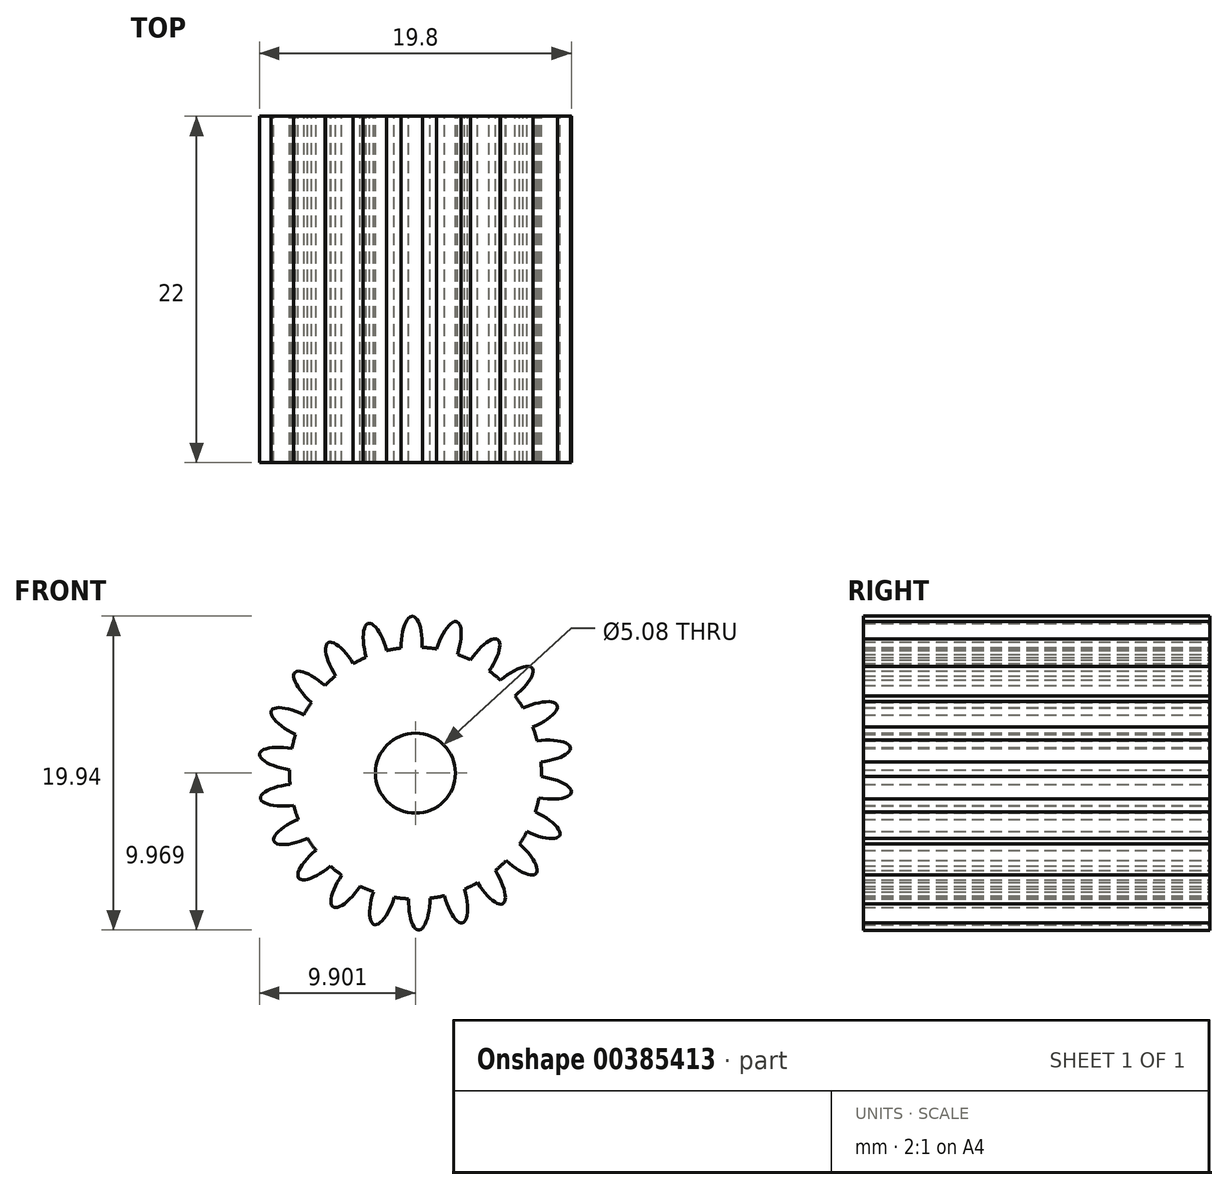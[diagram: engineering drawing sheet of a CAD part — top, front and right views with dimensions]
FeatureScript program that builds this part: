
annotation { "Feature Type Name" : "Feature", "Feature Type Description" : "" }
export const myFeature = defineFeature(function(context is Context, id is Id, definition is map)
    precondition{}
    {
        {
            var Q0;
            Q0=qCreatedBy(makeId("Front.planeOp"),FACE);
            var sketch = newSketch(context, id + "F0", { "sketchPlane" : qUnion([Q0])});
            skCircle(sketch, "E0", {"center": v(0.02, -0.42) * mm, "radius": 8 * mm});
            skLineSegment(sketch, "E1", {"start": v(0.02, -0.42) * mm, "end": v(-1.13, 7.5) * mm});
            skLineSegment(sketch, "E2", {"start": v(0.02, -0.42) * mm, "end": v(0.12, 7.58) * mm});
            skEllipticalArc(sketch, "E3.38.0", {});
            skCircle(sketch, "E4", {"center": v(0.02, -0.42) * mm, "radius": 2.54 * mm});
            skEllipticalArc(sketch, "E5.1.0", {});
            skEllipticalArc(sketch, "E5.2.0", {});
            skEllipticalArc(sketch, "E5.3.0", {});
            skEllipticalArc(sketch, "E5.4.0", {});
            skEllipticalArc(sketch, "E5.5.0", {});
            skEllipticalArc(sketch, "E5.6.0", {});
            skEllipticalArc(sketch, "E5.7.0", {});
            skEllipticalArc(sketch, "E5.8.0", {});
            skEllipticalArc(sketch, "E5.9.0", {});
            skEllipticalArc(sketch, "E5.10.0", {});
            skEllipticalArc(sketch, "E5.11.0", {});
            skEllipticalArc(sketch, "E5.12.0", {});
            skEllipticalArc(sketch, "E5.13.0", {});
            skEllipticalArc(sketch, "E5.14.0", {});
            skEllipticalArc(sketch, "E5.15.0", {});
            skEllipticalArc(sketch, "E5.16.0", {});
            skEllipticalArc(sketch, "E5.17.0", {});
            skEllipticalArc(sketch, "E5.18.0", {});
            skEllipticalArc(sketch, "E5.19.0", {});
            skEllipticalArc(sketch, "E5.20.0", {});
            skEllipticalArc(sketch, "E5.21.0", {});
            const initialGuessF0  = {"E3.38.0": [0.002036120399755269, 0.0073205969644864755, -0.3090169943749474, -0.9510565162951536, 0.0019768298493211675, 0.0006797314705727096, 1.5766588321977384, 4.747653305813112], "E5.1.0": [-0.00022669867967855563, 0.007574662292885675, -0.02855605079369622, -0.9995921928281893, 0.0019768298493211675, 0.0006797314705727096, 1.5766588321977386, 4.747653305813111], "E5.2.0": [-0.0024694361615308, 0.0071809263854053056, 0.25421833419348694, -0.9671468547019572, 0.0019768298493211675, 0.0006797314705727096, 1.5766588321977386, 4.747653305813111], "E5.3.0": [-0.004510398793095173, 0.006171287383631821, 0.5163974616389619, -0.856349030251589, 0.0019768298493211675, 0.0006797314705727096, 1.5766588321977386, 4.747653305813111], "E5.4.0": [-0.006184239920034473, 0.004627540234934563, 0.7367411378764049, -0.6761749002740194, 0.0019768298493211675, 0.0006797314705727096, 1.5766588321977386, 4.747653305813111], "E5.5.0": [-0.007355354888960557, 0.002674750152283181, 0.8973984286913584, -0.4412211012432212, 0.0019768298493211675, 0.0006797314705727096, 1.5766588321977386, 4.747653305813111], "E5.6.0": [-0.007928866929979935, 0.00047112057448429, 0.9853538358476931, -0.1705221926326239, 0.0019768298493211675, 0.0006797314705727096, 1.5766588321977386, 4.747653305813111], "E5.7.0": [-0.007858313508336654, -0.0018048235355585646, 0.9934817353485503, 0.11399140989054057, 0.0019768298493211675, 0.0006797314705727096, 1.5766588321977386, 4.747653305813111], "E5.8.0": [-0.0071494104426549, -0.003968698721610511, 0.9211236531148501, 0.38927010631739145, 0.0019768298493211675, 0.0006797314705727096, 1.5766588321977386, 4.747653305813111], "E5.9.0": [-0.005859588843307343, -0.005845200685158868, 0.7741416106390826, 0.6330124538088703, 0.0019768298493211675, 0.0006797314705727096, 1.5766588321977386, 4.747653305813111], "E5.10.0": [-0.004093342385408703, -0.007282306397103836, 0.5644432188667692, 0.825471896962774, 0.0019768298493211675, 0.0006797314705727096, 1.5766588321977386, 4.747653305813111], "E5.11.0": [-0.0019937618527057924, -0.00816359009946039, 0.30901699437494795, 0.9510565162951534, 0.0019768298493211675, 0.0006797314705727096, 1.5766588321977386, 4.747653305813111], "E5.12.0": [0.00026905722672803474, -0.00841765542785959, 0.028556050793696552, 0.9995921928281893, 0.0019768298493211675, 0.0006797314705727096, 1.5766588321977386, 4.747653305813111], "E5.13.0": [0.002511794708580281, -0.00802391952037922, -0.25421833419348694, 0.9671468547019572, 0.0019768298493211675, 0.0006797314705727096, 1.5766588321977386, 4.747653305813111], "E5.14.0": [0.004552757340144654, -0.007014280518605736, -0.5163974616389618, 0.856349030251589, 0.0019768298493211675, 0.0006797314705727096, 1.5766588321977386, 4.747653305813111], "E5.15.0": [0.00622659846708395, -0.005470533369908482, -0.7367411378764044, 0.67617490027402, 0.0019768298493211675, 0.0006797314705727096, 1.5766588321977386, 4.747653305813111], "E5.16.0": [0.007397713436010037, -0.003517743287257096, -0.8973984286913584, 0.44122110124322134, 0.0019768298493211675, 0.0006797314705727096, 1.5766588321977386, 4.747653305813111], "E5.17.0": [0.007971225477029416, -0.0013141137094582053, -0.9853538358476931, 0.170522192632624, 0.0019768298493211675, 0.0006797314705727096, 1.5766588321977386, 4.747653305813111], "E5.18.0": [0.007900672055386136, 0.000961830400584648, -0.9934817353485503, -0.11399140989054024, 0.0019768298493211675, 0.0006797314705727096, 1.5766588321977386, 4.747653305813111], "E5.19.0": [0.007191768989704384, 0.003125705586636593, -0.9211236531148503, -0.3892701063173909, 0.0019768298493211675, 0.0006797314705727096, 1.5766588321977386, 4.747653305813111], "E5.20.0": [0.005901947390356822, 0.005002207550184956, -0.7741416106390825, -0.6330124538088706, 0.0019768298493211675, 0.0006797314705727096, 1.5766588321977386, 4.747653305813111], "E5.21.0": [0.004135700932458185, 0.006439313262129921, -0.5644432188667692, -0.825471896962774, 0.0019768298493211675, 0.0006797314705727096, 1.5766588321977386, 4.747653305813111]};
            skSetInitialGuess(sketch, initialGuessF0);
            skSolve(sketch);
        }
        {
            var Q0;
            Q0 = qSketchRegion(id + "F0", true);
            extrude(context, id + "F1", {"entities" : qUnion([Q0]), "depth" : 22 * mm});
        }
    });
